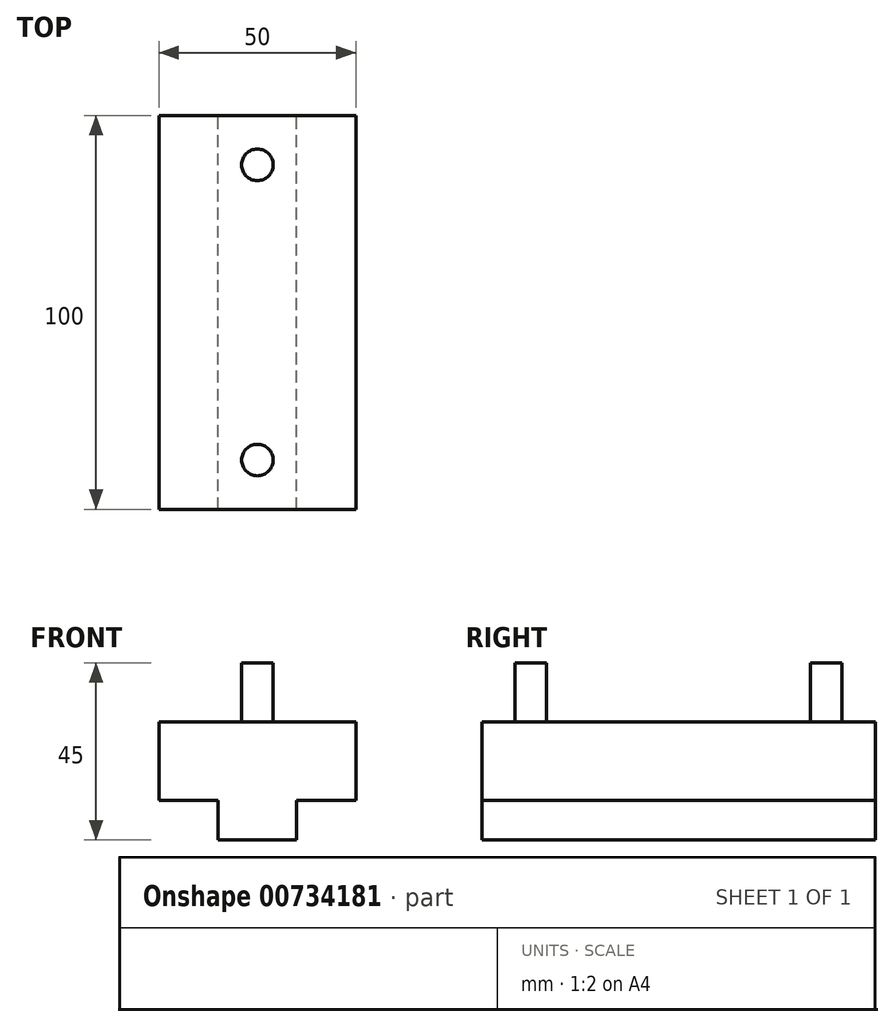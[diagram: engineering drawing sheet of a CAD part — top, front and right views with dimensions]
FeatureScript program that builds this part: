
annotation { "Feature Type Name" : "Feature", "Feature Type Description" : "" }
export const myFeature = defineFeature(function(context is Context, id is Id, definition is map)
    precondition{}
    {
        {
            var Q0;
            Q0=qCreatedBy(makeId("Front.planeOp"),FACE);
            var sketch = newSketch(context, id + "F0", { "sketchPlane" : qUnion([Q0])});
            skLineSegment(sketch, "E0.bottom", {"start": v(0, 0) * mm, "end": v(15, 0) * mm});
            skLineSegment(sketch, "E0.top", {"start": v(0, 20) * mm, "end": v(50, 20) * mm});
            skLineSegment(sketch, "E0.left", {"start": v(0, 0) * mm, "end": v(0, 20) * mm});
            skLineSegment(sketch, "E0.right", {"start": v(50, 0) * mm, "end": v(50, 20) * mm});
            skLineSegment(sketch, "E1", {"start": v(15, 0) * mm, "end": v(15, -10) * mm});
            skLineSegment(sketch, "E2", {"start": v(15, -10) * mm, "end": v(35, -10) * mm});
            skLineSegment(sketch, "E3", {"start": v(35, -10) * mm, "end": v(35, 0) * mm});
            skLineSegment(sketch, "E4.trimOffspring", {"start": v(35, 0) * mm, "end": v(50, 0) * mm});
            skLineSegment(sketch, "E5", {"start": v(25, 20) * mm, "end": v(25, -10) * mm, "construction": true});
            skSolve(sketch);
        }
        {
            var Q0;
            Q0 = qSketchRegion(id + "F0", true);
            extrude(context, id + "F1", {"entities" : qUnion([Q0]), "depth" : 100 * mm, "offsetDistance" : 25 * mm});
        }
        {
            var Q0;
            Q0=makeQuery(id+"F1.opExtrude","SWEPT_FACE",FACE,{"disambiguationData":[OSD([sQuery(id+"F0.wireOp",EDGE,"E0.top")])]});
            var sketch = newSketch(context, id + "F2", { "sketchPlane" : qUnion([Q0])});
            skLineSegment(sketch, "E6", {"start": v(0, -50) * mm, "end": v(50, -50) * mm, "construction": true});
            skCircle(sketch, "E7", {"center": v(25, -12.5) * mm, "radius": 4 * mm});
            skCircle(sketch, "E8", {"center": v(25, -87.5) * mm, "radius": 4 * mm});
            skSolve(sketch);
        }
        {
            var Q0;
            Q0 = qSketchRegion(id + "F2", true);
            extrude(context, id + "F3", {"entities" : qUnion([Q0]), "operationType" : NewBodyOperationType.ADD, "depth" : 15 * mm, "offsetDistance" : 25 * mm});
        }
    });
